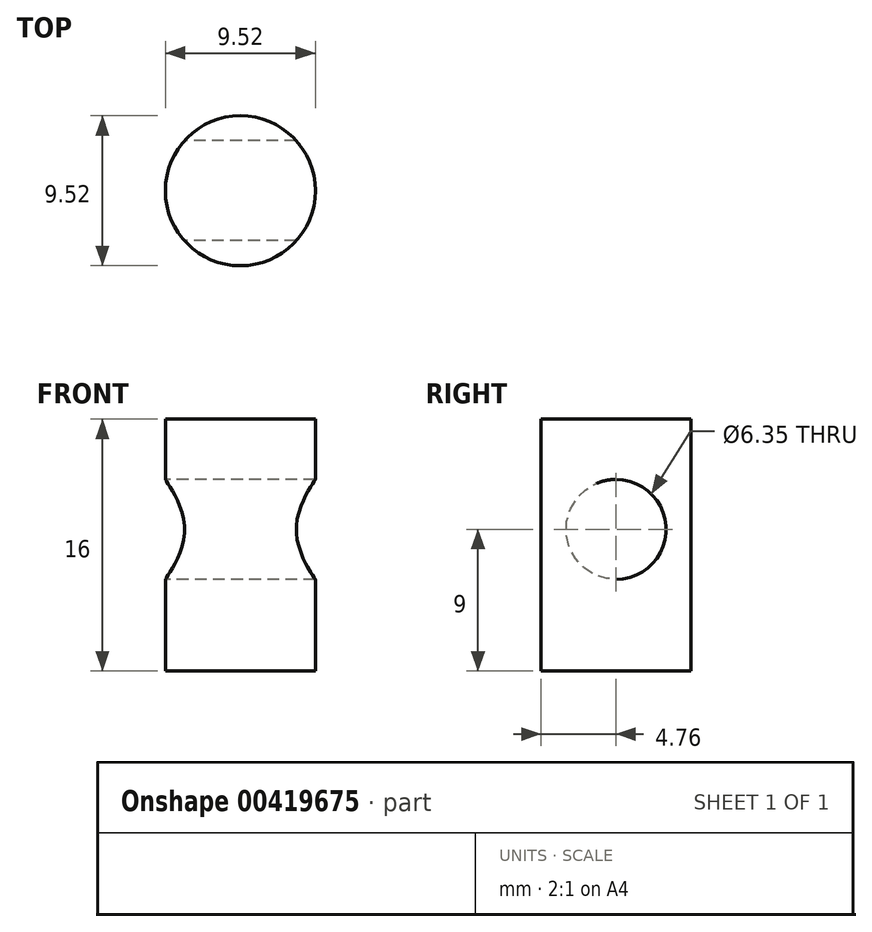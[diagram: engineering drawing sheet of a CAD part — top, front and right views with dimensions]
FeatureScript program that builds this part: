
annotation { "Feature Type Name" : "Feature", "Feature Type Description" : "" }
export const myFeature = defineFeature(function(context is Context, id is Id, definition is map)
    precondition{}
    {
        {
            var Q0;
            Q0=qCreatedBy(makeId("Top.planeOp"),FACE);
            var sketch = newSketch(context, id + "F0", { "sketchPlane" : qUnion([Q0])});
            skCircle(sketch, "E0", {"center": v(0, 0) * mm, "radius": 4.76 * mm});
            skSolve(sketch);
        }
        {
            var Q0;
            Q0 = qSketchRegion(id + "F0", true);
            extrude(context, id + "F1", {"entities" : qUnion([Q0]), "depth" : 16 * mm, "offsetDistance" : 25.4 * mm});
        }
        {
            var Q0;
            Q0=qCreatedBy(makeId("Right.planeOp"),FACE);
            var sketch = newSketch(context, id + "F2", { "sketchPlane" : qUnion([Q0])});
            skCircle(sketch, "E1", {"center": v(0, 9) * mm, "radius": 3.18 * mm});
            skSolve(sketch);
        }
        {
            var Q0;
            Q0 = qSketchRegion(id + "F2", true);
            extrude(context, id + "F3", {"entities" : qUnion([Q0]), "operationType" : NewBodyOperationType.REMOVE, "depth" : 25.4 * mm, "offsetDistance" : 25.4 * mm, "hasSecondDirection" : true, "secondDirectionOppositeDirection" : true, "secondDirectionDepth" : 25.4 * mm});
        }
    });
